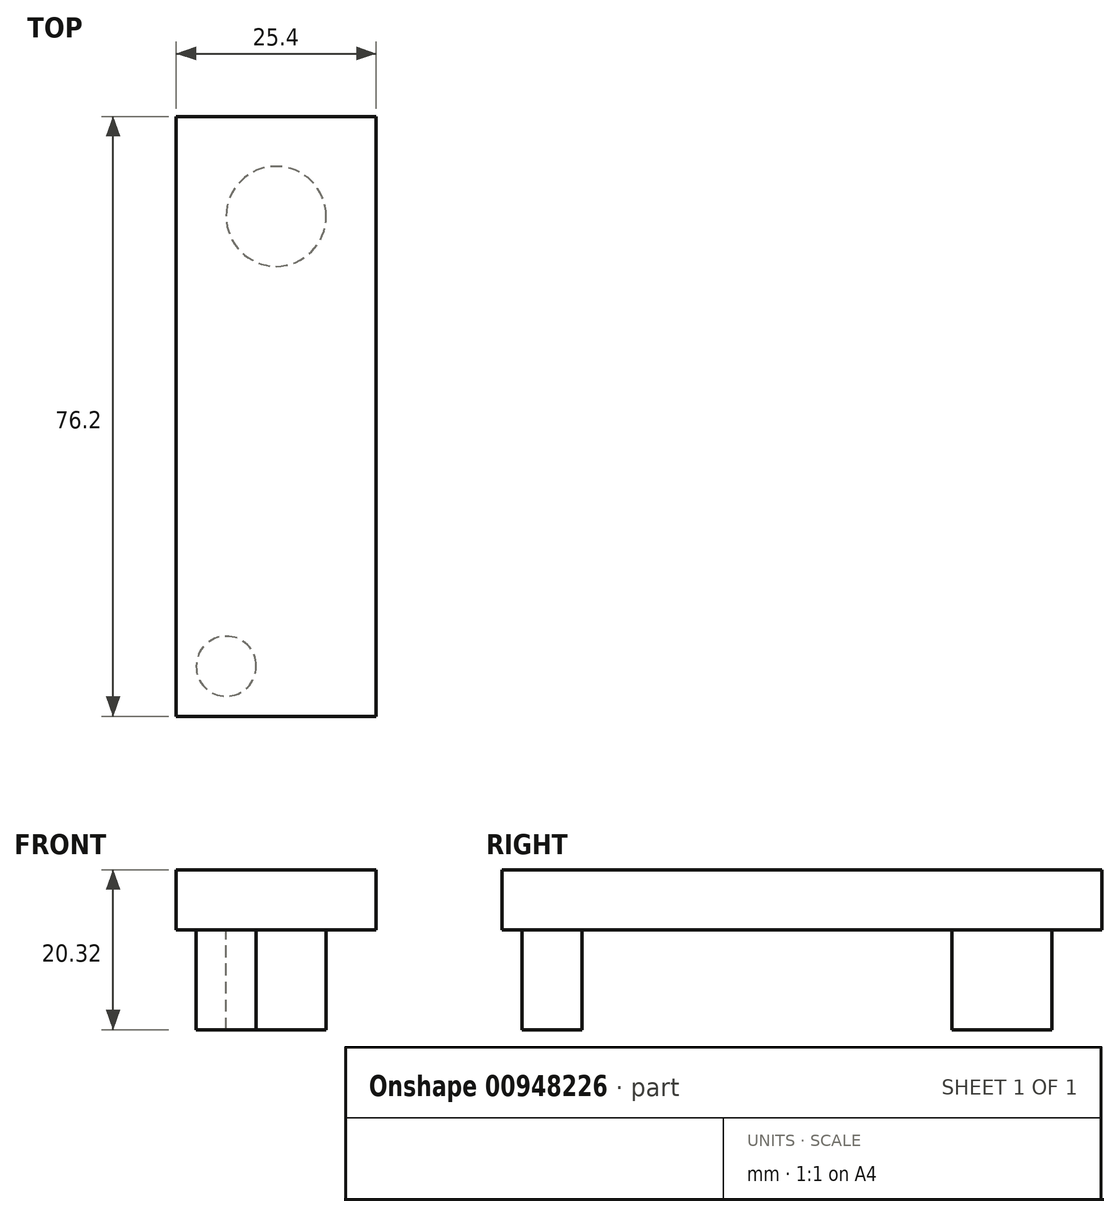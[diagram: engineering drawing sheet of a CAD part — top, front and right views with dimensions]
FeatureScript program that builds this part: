
annotation { "Feature Type Name" : "Feature", "Feature Type Description" : "" }
export const myFeature = defineFeature(function(context is Context, id is Id, definition is map)
    precondition{}
    {
        {
            var Q0;
            Q0=qCreatedBy(makeId("Top.planeOp"),FACE);
            var sketch = newSketch(context, id + "F0", { "sketchPlane" : qUnion([Q0])});
            skLineSegment(sketch, "E0.bottom", {"start": v(-13.73, 34.67) * mm, "end": v(11.67, 34.67) * mm});
            skLineSegment(sketch, "E0.top", {"start": v(-13.73, -41.53) * mm, "end": v(11.67, -41.53) * mm});
            skLineSegment(sketch, "E0.left", {"start": v(-13.73, 34.67) * mm, "end": v(-13.73, -41.53) * mm});
            skLineSegment(sketch, "E1", {"start": v(11.67, 34.67) * mm, "end": v(11.67, -41.53) * mm});
            skSolve(sketch);
        }
        {
            var Q0;
            Q0=makeQuery(id+"F0.imprint","IMPRINT",FACE,{"disambiguationData":[TD([[makeQuery(id+"F0.imprint","IMPRINT",EDGE,{"derivedFrom":sQuery(id+"F0.wireOp",EDGE,"E0.bottom")}),-1.0]])]});
            extrude(context, id + "F1", {"entities" : qUnion([Q0]), "depth" : 7.62 * mm, "offsetDistance" : 25.4 * mm});
        }
        {
            var Q0;
            Q0=makeQuery(id+"F1.opExtrude","CAP_FACE",FACE,{"disambiguationData":[OSD([sQuery(id+"F0.wireOp",EDGE,"E0.bottom"),sQuery(id+"F0.wireOp",EDGE,"E0.top"),sQuery(id+"F0.wireOp",EDGE,"E0.left"),sQuery(id+"F0.wireOp",EDGE,"E1")])],"isStart":true});
            var sketch = newSketch(context, id + "F2", { "sketchPlane" : qUnion([Q0])});
            skCircle(sketch, "E2", {"center": v(-1.03, -21.97) * mm, "radius": 6.35 * mm});
            skSolve(sketch);
        }
        {
            var Q0;
            Q0=makeQuery(id+"F2.imprint","IMPRINT",FACE,{"disambiguationData":[TD([[makeQuery(id+"F2.imprint","IMPRINT",EDGE,{"derivedFrom":sQuery(id+"F2.wireOp",EDGE,"E2")}),1.0]])]});
            extrude(context, id + "F3", {"entities" : qUnion([Q0]), "operationType" : NewBodyOperationType.ADD, "depth" : 12.7 * mm, "offsetDistance" : 25.4 * mm});
        }
        {
            var Q0;
            Q0=makeQuery(id+"F1.opExtrude","CAP_FACE",FACE,{"disambiguationData":[OSD([sQuery(id+"F0.wireOp",EDGE,"E0.bottom"),sQuery(id+"F0.wireOp",EDGE,"E0.top"),sQuery(id+"F0.wireOp",EDGE,"E0.left"),sQuery(id+"F0.wireOp",EDGE,"E1")])],"isStart":true});
            var sketch = newSketch(context, id + "F4", { "sketchPlane" : qUnion([Q0])});
            skCircle(sketch, "E3", {"center": v(-1.03, -21.97) * mm, "radius": 12.7 * mm});
            skPoint(sketch, "E4.3.internal.snap0", {"position": v(-1.03, 41.53) * mm});
            skFitSpline(sketch, "E4", {"points": [v(-13.73, -21.97) * mm, v(-11.62, -4.88) * mm, v(-7.97, 13.31) * mm, v(-1.03, 26.54) * mm, v(11.67, 38.26) * mm], "startDerivative": vector(7.77, 70.85) * mm, "endDerivative": vector(69.45, 29.16) * mm});
            skLineSegment(sketch, "E5", {"start": v(11.67, 38.26) * mm, "end": v(11.67, 41.53) * mm});
            skLineSegment(sketch, "E6", {"start": v(11.67, 41.53) * mm, "end": v(-13.73, 41.53) * mm});
            skLineSegment(sketch, "E7", {"start": v(-13.73, 41.53) * mm, "end": v(-13.73, -21.97) * mm});
            skSolve(sketch);
        }
        {
            var Q0;
            {var subQ0=sQuery(id+"F4.wireOp",EDGE,"E5");Q0=makeQuery(id+"F4.imprint","IMPRINT",FACE,{"disambiguationData":[TD([[makeQuery(id+"F4.imprint","IMPRINT",EDGE,{"derivedFrom":subQ0}),1.0]])]});}
            extrude(context, id + "F5", {"entities" : qUnion([Q0]), "operationType" : NewBodyOperationType.ADD, "depth" : 7.62 * mm, "offsetDistance" : 25.4 * mm});
        }
        {
            var Q0;
            Q0=makeQuery(id+"F5.opExtrude","CAP_FACE",FACE,{"disambiguationData":[OSD([sQuery(id+"F4.wireOp",EDGE,"E3"),sQuery(id+"F4.wireOp",EDGE,"E4"),sQuery(id+"F4.wireOp",EDGE,"E5"),sQuery(id+"F4.wireOp",EDGE,"E6"),sQuery(id+"F4.wireOp",EDGE,"E7")])],"isStart":false});
            var sketch = newSketch(context, id + "F6", { "sketchPlane" : qUnion([Q0])});
            skCircle(sketch, "E8", {"center": v(-7.38, 35.18) * mm, "radius": 3.81 * mm});
            skSolve(sketch);
        }
        {
            var Q0;
            Q0=makeQuery(id+"F6.imprint","IMPRINT",FACE,{"disambiguationData":[TD([[makeQuery(id+"F6.imprint","IMPRINT",EDGE,{"derivedFrom":sQuery(id+"F6.wireOp",EDGE,"E8")}),-1.0]])]});
            extrude(context, id + "F7", {"entities" : qUnion([Q0]), "operationType" : NewBodyOperationType.REMOVE, "oppositeDirection" : true, "depth" : 7.62 * mm, "offsetDistance" : 25.4 * mm});
        }
        {
            var Q0;
            Q0=makeQuery(id+"F5.opExtrude","CAP_FACE",FACE,{"disambiguationData":[OSD([sQuery(id+"F4.wireOp",EDGE,"E3"),sQuery(id+"F4.wireOp",EDGE,"E4"),sQuery(id+"F4.wireOp",EDGE,"E5"),sQuery(id+"F4.wireOp",EDGE,"E6"),sQuery(id+"F4.wireOp",EDGE,"E7")])],"isStart":false});
            extrude(context, id + "F8", {"entities" : qUnion([Q0]), "operationType" : NewBodyOperationType.ADD, "depth" : 5.08 * mm, "offsetDistance" : 25.4 * mm});
        }
    });
